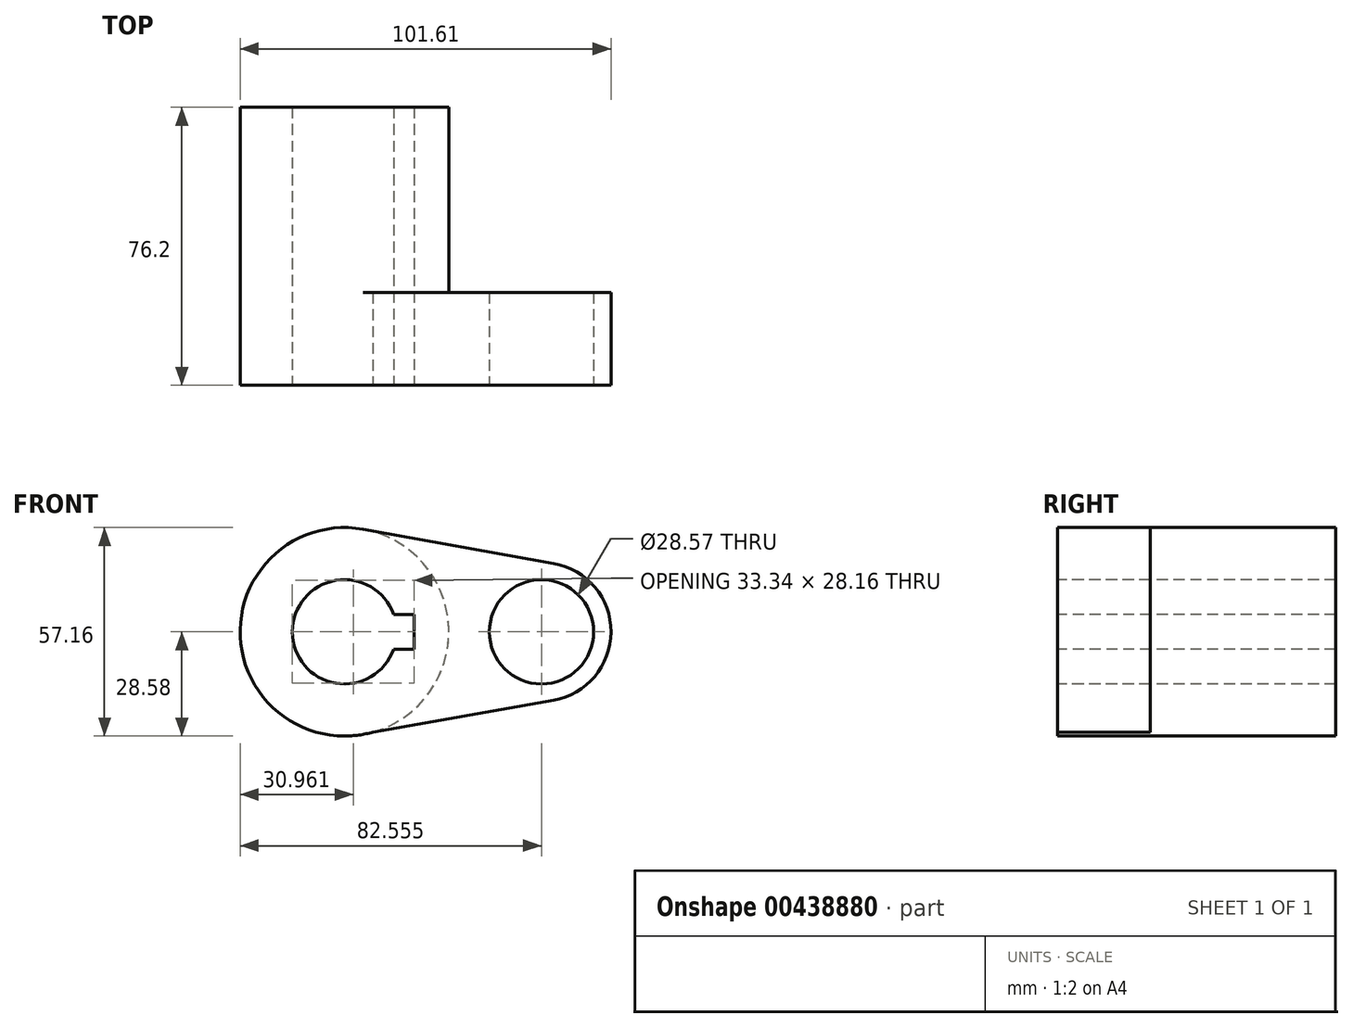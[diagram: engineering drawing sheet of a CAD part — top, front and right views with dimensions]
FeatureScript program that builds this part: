
annotation { "Feature Type Name" : "Feature", "Feature Type Description" : "" }
export const myFeature = defineFeature(function(context is Context, id is Id, definition is map)
    precondition{}
    {
        {
            var Q0;
            Q0=qCreatedBy(makeId("Front.planeOp"),FACE);
            var sketch = newSketch(context, id + "F0", { "sketchPlane" : qUnion([Q0])});
            skCircle(sketch, "E0", {"center": v(0, 0) * mm, "radius": 28.58 * mm});
            skCircle(sketch, "E1", {"center": v(53.98, 0) * mm, "radius": 19.05 * mm});
            skLineSegment(sketch, "E2", {"start": v(5.04, 28.13) * mm, "end": v(57.34, 18.75) * mm});
            skLineSegment(sketch, "E3", {"start": v(7.83, -27.48) * mm, "end": v(57.28, -18.76) * mm});
            skCircle(sketch, "E4", {"center": v(0, 0) * mm, "radius": 14.29 * mm});
            skCircle(sketch, "E5", {"center": v(53.98, 0) * mm, "radius": 14.29 * mm});
            skLineSegment(sketch, "E6.bottom", {"start": v(19.05, -4.76) * mm, "end": v(-19.05, -4.76) * mm});
            skLineSegment(sketch, "E6.top", {"start": v(19.05, 4.76) * mm, "end": v(-19.05, 4.76) * mm});
            skLineSegment(sketch, "E6.left", {"start": v(19.05, -4.76) * mm, "end": v(19.05, 4.76) * mm});
            skLineSegment(sketch, "E6.right", {"start": v(-19.05, -4.76) * mm, "end": v(-19.05, 4.76) * mm});
            skSolve(sketch);
        }
        {
            var Q0;
            {var subQ5=sQuery(id+"F0.wireOp",EDGE,"E6.right");Q0=makeQuery(id+"F0.imprint","IMPRINT",FACE,{"disambiguationData":[TD([[makeQuery(id+"F0.imprint","IMPRINT",EDGE,{"derivedFrom":subQ5}),-1.0]])]});}
            var Q1;
            {var subQ7=sQuery(id+"F0.wireOp",EDGE,"E6.left");Q1=makeQuery(id+"F0.imprint","IMPRINT",FACE,{"disambiguationData":[TD([[makeQuery(id+"F0.imprint","IMPRINT",EDGE,{"derivedFrom":subQ7}),-1.0]])]});}
            extrude(context, id + "F1", {"entities" : qUnion([Q0, Q1]), "oppositeDirection" : true, "depth" : 50.8 * mm});
        }
        {
            var Q0;
            Q0=makeQuery(id+"F1.opExtrude","CAP_FACE",FACE,{"disambiguationData":[OSD([sQuery(id+"F0.wireOp",EDGE,"E0"),sQuery(id+"F0.wireOp",EDGE,"E1"),sQuery(id+"F0.wireOp",EDGE,"E2"),sQuery(id+"F0.wireOp",EDGE,"E3"),sQuery(id+"F0.wireOp",EDGE,"E4"),sQuery(id+"F0.wireOp",EDGE,"E5"),sQuery(id+"F0.wireOp",EDGE,"E6.bottom"),sQuery(id+"F0.wireOp",EDGE,"E6.top"),sQuery(id+"F0.wireOp",EDGE,"E6.left"),sQuery(id+"F0.wireOp",EDGE,"E6.right")])],"isStart":false});
            var Q1;
            Q1=makeQuery(id+"F0.imprint","IMPRINT",FACE,{"disambiguationData":[TD([[makeQuery(id+"F0.imprint","IMPRINT",EDGE,{"derivedFrom":sQuery(id+"F0.wireOp",EDGE,"E5")}),-1.0]])]});
            var Q2;
            {var subQ0=sQuery(id+"F0.wireOp",EDGE,"E2");Q2=makeQuery(id+"F0.imprint","IMPRINT",FACE,{"disambiguationData":[TD([[makeQuery(id+"F0.imprint","IMPRINT",EDGE,{"derivedFrom":subQ0}),-1.0]])]});}
            extrude(context, id + "F2", {"entities" : qUnion([Q0, Q1, Q2]), "operationType" : NewBodyOperationType.ADD, "depth" : 25.4 * mm});
        }
    });
